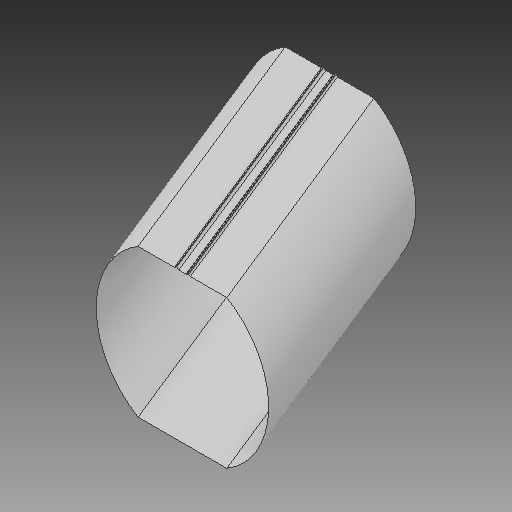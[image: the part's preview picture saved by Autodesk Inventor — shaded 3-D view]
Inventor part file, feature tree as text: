
AUTODESK INVENTOR PART (.ipt)
format: ipt  version: 2017 (Build 210142000, 142)  size: 148,992 bytes
history: native  units: in
note: dims shown in document units (in); Inventor stores cm internally (conversion verified against a paired STEP export)
features: sketch x2, other x1, plane x1, delete_face x1
ambient origin geometry x8: Origin, YZ Plane, XZ Plane, XY Plane, X Axis, Y Axis, Z Axis, Center Point
bodies: Solid1 (feature_tree)
feature tree (5):
  other  "ramp"
  sketch  "Sketch1"  dims[d28=8.0in]
  plane  "Work Plane2"
  delete_face  "Delete Face1"
  sketch  "Sketch6"  dims[d30=0.0in d31=0.0in d59=3.3333in d61=3.3333in d62=0.8521in d63=4.0in d64=0.5833in d65=3.8873in d66=3.8873in d67=1.7083in d68=0.0625in d69=0.0625in d70=1.6458in d71=0.25in d72=0.125in d74=0.0884in d75=45.0deg d76=3.3333in d77=0.125in]
